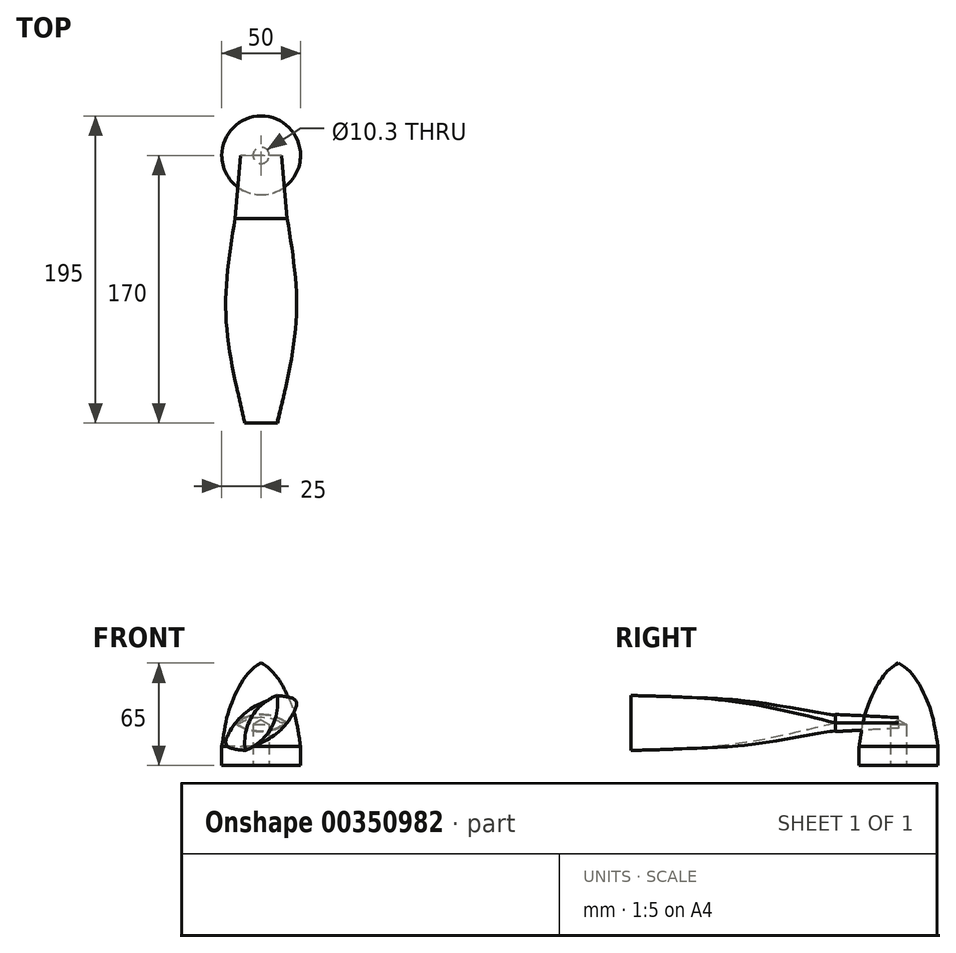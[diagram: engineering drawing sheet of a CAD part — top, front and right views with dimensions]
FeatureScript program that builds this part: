
annotation { "Feature Type Name" : "Feature", "Feature Type Description" : "" }
export const myFeature = defineFeature(function(context is Context, id is Id, definition is map)
    precondition{}
    {
        {
            var Q0;
            Q0=qCreatedBy(makeId("Front.planeOp"),FACE);
            var sketch = newSketch(context, id + "F0", { "sketchPlane" : qUnion([Q0])});
            skLineSegment(sketch, "E0", {"start": v(0, 0) * mm, "end": v(25, 0) * mm});
            skLineSegment(sketch, "E1", {"start": v(25, 0) * mm, "end": v(25, 12) * mm});
            skLineSegment(sketch, "E2", {"start": v(0, 0) * mm, "end": v(0, 65) * mm});
            skFitSpline(sketch, "E3", {"points": [v(0, 65) * mm, v(17.34, 43) * mm, v(25, 12) * mm], "startDerivative": vector(55.16, -26.79) * mm, "endDerivative": vector(14.88, -105.54) * mm});
            skSolve(sketch);
        }
        {
            var Q0;
            Q0 = qSketchRegion(id + "F0", true);
            var Q1;
            Q1=sQuery(id+"F0.wireOp",EDGE,"E2");
            revolve(context, id + "F1", {"entities" : qUnion([Q0]), "axis" : qUnion([Q1]), "revolveType" : RevolveType.FULL});
        }
        {
            var Q0;
            Q0=makeQuery(id+"F1.opRevolve","SWEPT_FACE",FACE,{"disambiguationData":[OSD([sQuery(id+"F0.wireOp",EDGE,"E0")])]});
            var sketch = newSketch(context, id + "F2", { "sketchPlane" : qUnion([Q0])});
            skPoint(sketch, "E4", {"position": v(0, 0) * mm});
            skSolve(sketch);
        }
        {
            var Q0;
            Q0=qCreatedBy(makeId("Front.planeOp"),FACE);
            cPlane(context, id + "F3", {"entities" : qUnion([Q0]), "cplaneType" : CPlaneType.OFFSET, "offset" : 40 * mm, "width" : 150 * mm, "height" : 150 * mm});
        }
        {
            var Q0;
            Q0=qCreatedBy(id+"F3.planeOp",FACE);
            cPlane(context, id + "F4", {"entities" : qUnion([Q0]), "cplaneType" : CPlaneType.OFFSET, "offset" : 60 * mm, "width" : 150 * mm, "height" : 150 * mm});
        }
        {
            var Q0;
            Q0=qCreatedBy(id+"F4.planeOp",FACE);
            cPlane(context, id + "F5", {"entities" : qUnion([Q0]), "cplaneType" : CPlaneType.OFFSET, "offset" : 70 * mm, "width" : 150 * mm, "height" : 150 * mm});
        }
        {
            var Q0;
            Q0=qCreatedBy(id+"F3.planeOp",FACE);
            var sketch = newSketch(context, id + "F6", { "sketchPlane" : qUnion([Q0])});
            skLineSegment(sketch, "E5", {"start": v(0, 67.03) * mm, "end": v(0, -4.37) * mm, "construction": true});
            skLineSegment(sketch, "E6", {"start": v(-66.14, 27) * mm, "end": v(61.58, 27) * mm, "construction": true});
            skArc(sketch, "E7", {"start": v(16.58, 27) * mm, "mid": v(0, 32) * mm, "end": v(-16.58, 27) * mm});
            skArc(sketch, "E8.MirrorCS", {"start": v(16.58, 27) * mm, "mid": v(0, 22) * mm, "end": v(-16.58, 27) * mm});
            skSolve(sketch);
        }
        {
            var Q0;
            Q0=qCreatedBy(id+"F4.planeOp",FACE);
            var sketch = newSketch(context, id + "F7", { "sketchPlane" : qUnion([Q0])});
            skArc(sketch, "E9.0", {"start": v(22.44, 39.95) * mm, "mid": v(-5.5, 36.53) * mm, "end": v(-22.42, 14.05) * mm});
            skArc(sketch, "E9.1", {"start": v(22.44, 39.95) * mm, "mid": v(5.5, 17.48) * mm, "end": v(-22.42, 14.05) * mm});
            skSolve(sketch);
        }
        {
            var Q0;
            Q0=qCreatedBy(id+"F5.planeOp",FACE);
            var sketch = newSketch(context, id + "F8", { "sketchPlane" : qUnion([Q0])});
            skLineSegment(sketch, "E10", {"start": v(-16.58, 27) * mm, "end": v(16.58, 27) * mm, "construction": true});
            skLineSegment(sketch, "E11", {"start": v(0, 22) * mm, "end": v(0, 32) * mm, "construction": true});
            skArc(sketch, "E12.0", {"start": v(10.07, 44.44) * mm, "mid": v(-6.15, 30.55) * mm, "end": v(-10.07, 9.56) * mm});
            skArc(sketch, "E12.1", {"start": v(10.07, 44.44) * mm, "mid": v(6.15, 23.45) * mm, "end": v(-10.07, 9.56) * mm});
            skSolve(sketch);
        }
        {
            var Q0;
            Q0 = qSketchRegion(id + "F6", true);
            var Q1;
            Q1 = qSketchRegion(id + "F7", true);
            var Q2;
            Q2 = qSketchRegion(id + "F8", true);
            loft(context, id + "F9", {"sheetProfilesArray" : [{ "sheetProfileEntities" : qUnion([Q0]) }, { "sheetProfileEntities" : qUnion([Q1]) }, { "sheetProfileEntities" : qUnion([Q2]) }]});
        }
        {
            var Q0;
            Q0=qCreatedBy(makeId("Front.planeOp"),FACE);
            var sketch = newSketch(context, id + "F10", { "sketchPlane" : qUnion([Q0])});
            skFitSpline(sketch, "E13.0", {"points": [v(15.48, 25.33) * mm, v(13.2, 26.84) * mm, v(8.2, 29.2) * mm, v(0, 30.4) * mm, v(-8.2, 29.2) * mm, v(-13.2, 26.84) * mm, v(-15.48, 25.33) * mm]});
            skFitSpline(sketch, "E13.1", {"points": [v(-15.48, 28.67) * mm, v(-13.2, 27.16) * mm, v(-8.2, 24.8) * mm, v(0, 23.6) * mm, v(8.2, 24.8) * mm, v(13.2, 27.16) * mm, v(15.48, 28.67) * mm]});
            skSolve(sketch);
        }
        {
            var Q0;
            Q0=makeQuery(id+"F9.opLoft","CAP_FACE",FACE,{"disambiguationData":[OSD([makeQuery(id+"F6.imprint","IMPRINT",FACE,{"disambiguationData":[TD([[makeQuery(id+"F6.imprint","IMPRINT",EDGE,{"derivedFrom":sQuery(id+"F6.wireOp",EDGE,"E7")}),1.0]])]})])],"isStart":true});
            var sketch = newSketch(context, id + "F11", { "sketchPlane" : qUnion([Q0])});
            skFitSpline(sketch, "E14.0", {"points": [v(-16.58, 27) * mm, v(-14.14, 28.62) * mm, v(-8.78, 31.14) * mm, v(0, 32.43) * mm, v(8.78, 31.14) * mm, v(14.14, 28.62) * mm, v(16.58, 27) * mm]});
            skFitSpline(sketch, "E15.0", {"points": [v(16.58, 27) * mm, v(14.14, 25.38) * mm, v(8.78, 22.86) * mm, v(0, 21.57) * mm, v(-8.78, 22.86) * mm, v(-14.14, 25.38) * mm, v(-16.58, 27) * mm]});
            skSolve(sketch);
        }
        {
            var Q1;
            Q1 = qSketchRegion(id + "F11", true);
            var Q2;
            Q2 = qSketchRegion(id + "F10", true);
            loft(context, id + "F12", {"sheetProfilesArray" : [{ "sheetProfileEntities" : qUnion([Q1]) }, { "sheetProfileEntities" : qUnion([Q2]) }]});
        }
        {
            var Q0;
            Q0=sQuery(id+"F2.wireOp",VERTEX,"E4");
            var Q1;
            Q1=makeQuery(id+"F1.opRevolve","SWEPT_BODY",BODY,{"disambiguationData":[OSD([sQuery(id+"F0.wireOp",EDGE,"E0"),sQuery(id+"F0.wireOp",EDGE,"E1"),sQuery(id+"F0.wireOp",EDGE,"E2"),sQuery(id+"F0.wireOp",EDGE,"E3")])]});
            hole(context, id + "F13", {"style" : HoleStyle.SIMPLE, "endStyle" : HoleEndStyle.BLIND, "standardTappedOrClearance" : lookupTablePath({ "standard" : "ISO", "engagement" : "75%", "pitch" : "1.75 mm", "size" : "M12", "type" : "Tapped" }), "standardBlindInLast" : lookupTablePath({ "standard" : "ISO", "engagement" : "75%", "pitch" : "1.75 mm", "size" : "M12", "type" : "Tapped" }), "holeDiameter" : 10.3 * mm, "showTappedDepth" : true, "holeDepth" : 26 * mm, "tappedDepth" : 20.75 * mm, "tapClearance" : 3, "startFromSketch" : true, "locations" : qUnion([Q0]), "scope" : qUnion([Q1]), "majorDiameter" : 12 * mm});
        }
        {
            var Q0;
            Q0=qCreatedBy(makeId("Front.planeOp"),FACE);
            var sketch = newSketch(context, id + "F14", { "sketchPlane" : qUnion([Q0])});
            skLineSegment(sketch, "E16", {"start": v(0, 0) * mm, "end": v(0, 89.99) * mm, "construction": true});
            skSolve(sketch);
        }
    });
